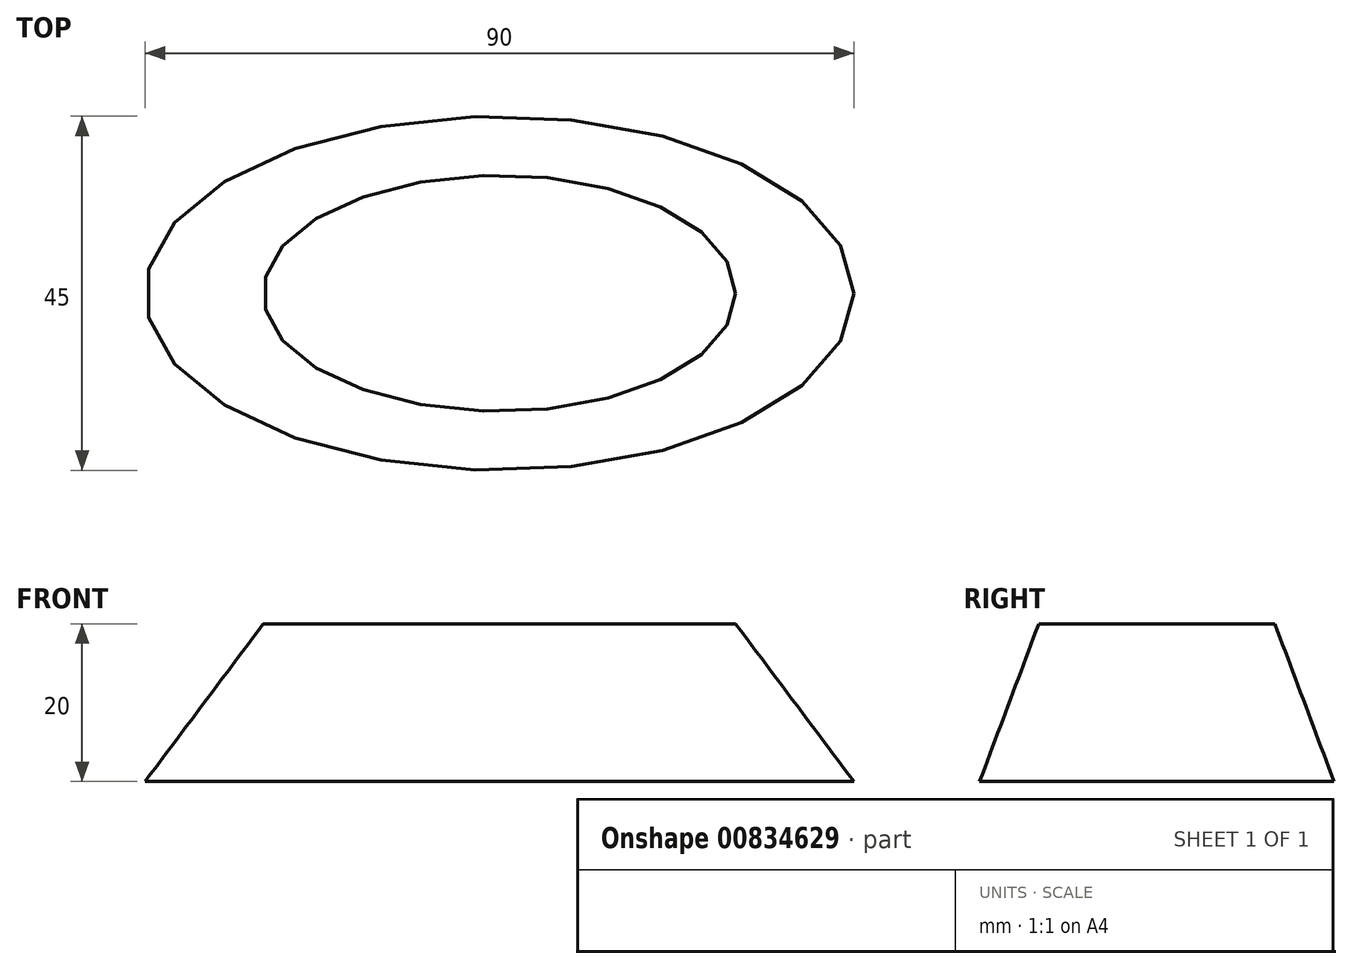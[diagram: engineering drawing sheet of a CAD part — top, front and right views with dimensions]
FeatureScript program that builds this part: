
annotation { "Feature Type Name" : "Feature", "Feature Type Description" : "" }
export const myFeature = defineFeature(function(context is Context, id is Id, definition is map)
    precondition{}
    {
        {
            var Q0;
            Q0=qCreatedBy(makeId("Top.planeOp"),FACE);
            var sketch = newSketch(context, id + "F0", { "sketchPlane" : qUnion([Q0])});
            skEllipse(sketch, "E0", {"center": v(0, 0) * mm, "majorRadius": 45 * mm, "minorRadius": 22.5 * mm, "majorAxis": v(1, 0)});
            skSolve(sketch);
        }
        {
            var Q0;
            Q0=qCreatedBy(makeId("Top.planeOp"),FACE);
            cPlane(context, id + "F1", {"entities" : qUnion([Q0]), "cplaneType" : CPlaneType.OFFSET, "offset" : 20 * mm, "width" : 150 * mm, "height" : 150 * mm});
        }
        {
            var Q0;
            Q0=qCreatedBy(id+"F1.planeOp",FACE);
            var sketch = newSketch(context, id + "F2", { "sketchPlane" : qUnion([Q0])});
            skEllipse(sketch, "E1", {"center": v(0, 0) * mm, "majorRadius": 30 * mm, "minorRadius": 15 * mm, "majorAxis": v(1, 0)});
            skSolve(sketch);
        }
        {
            var Q0;
            Q0 = qSketchRegion(id + "F0", true);
            var Q1;
            Q1 = qSketchRegion(id + "F2", true);
            loft(context, id + "F3", {"sheetProfilesArray" : [{ "sheetProfileEntities" : qUnion([Q0]) }, { "sheetProfileEntities" : qUnion([Q1]) }]});
        }
    });
